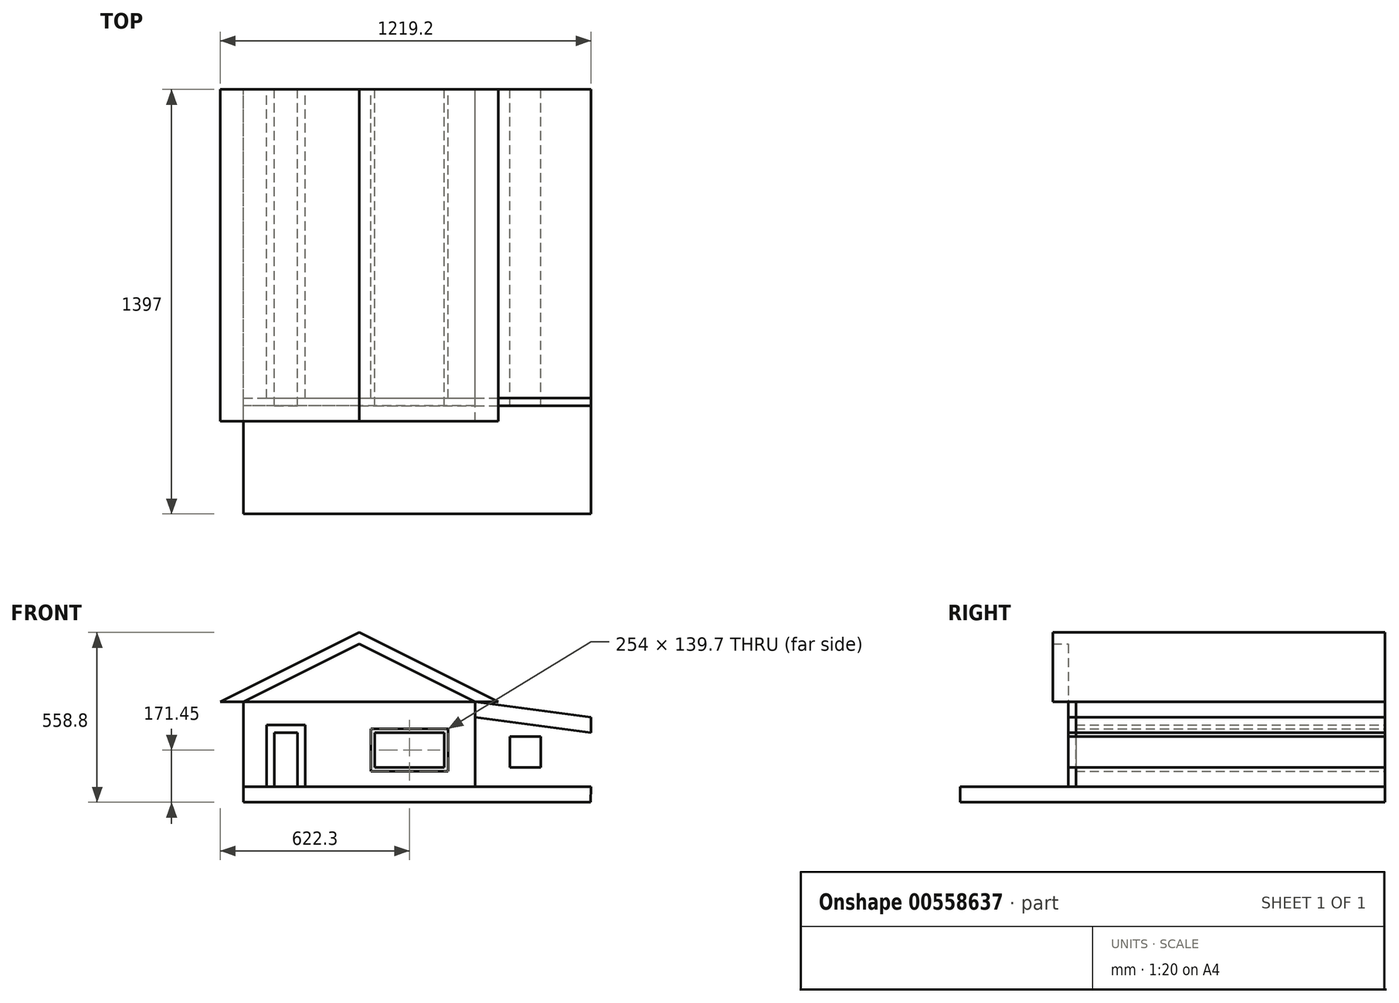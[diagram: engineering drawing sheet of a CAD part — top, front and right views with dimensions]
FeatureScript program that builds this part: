
annotation { "Feature Type Name" : "Feature", "Feature Type Description" : "" }
export const myFeature = defineFeature(function(context is Context, id is Id, definition is map)
    precondition{}
    {
        {
            var Q0;
            Q0=qCreatedBy(makeId("Front.planeOp"),FACE);
            var sketch = newSketch(context, id + "F0", { "sketchPlane" : qUnion([Q0])});
            skLineSegment(sketch, "E0", {"start": v(0, 0) * mm, "end": v(381, 0) * mm});
            skLineSegment(sketch, "E1", {"start": v(0, 0) * mm, "end": v(-381, 0) * mm});
            skLineSegment(sketch, "E2.bottom", {"start": v(-381, 0) * mm, "end": v(381, 0) * mm});
            skLineSegment(sketch, "E2.top", {"start": v(-381, -279.4) * mm, "end": v(381, -279.4) * mm});
            skLineSegment(sketch, "E2.left", {"start": v(-381, 0) * mm, "end": v(-381, -279.4) * mm});
            skLineSegment(sketch, "E2.right", {"start": v(381, 0) * mm, "end": v(381, -279.4) * mm});
            skLineSegment(sketch, "E3", {"start": v(0, 0) * mm, "end": v(0, 190.5) * mm});
            skLineSegment(sketch, "E4", {"start": v(0, 190.5) * mm, "end": v(-381, 0) * mm});
            skLineSegment(sketch, "E5", {"start": v(0, 190.5) * mm, "end": v(381, 0) * mm});
            skLineSegment(sketch, "E6", {"start": v(0, 190.5) * mm, "end": v(0, 228.6) * mm});
            skLineSegment(sketch, "E7", {"start": v(-381, 0) * mm, "end": v(-457.2, 0) * mm});
            skLineSegment(sketch, "E8", {"start": v(381, 0) * mm, "end": v(457.2, 0) * mm});
            skLineSegment(sketch, "E9", {"start": v(457.2, 0) * mm, "end": v(0, 228.6) * mm});
            skLineSegment(sketch, "E10", {"start": v(0, 228.6) * mm, "end": v(-457.2, 0) * mm});
            skLineSegment(sketch, "E11", {"start": v(-279.4, -279.4) * mm, "end": v(-279.4, -101.6) * mm});
            skLineSegment(sketch, "E12", {"start": v(-203.2, -279.4) * mm, "end": v(-203.2, -101.6) * mm});
            skLineSegment(sketch, "E13", {"start": v(-279.4, -101.6) * mm, "end": v(-203.2, -101.6) * mm});
            skLineSegment(sketch, "E14.0", {"start": v(-177.8, -279.4) * mm, "end": v(-177.8, -76.2) * mm});
            skLineSegment(sketch, "E14.1", {"start": v(-304.8, -76.2) * mm, "end": v(-177.8, -76.2) * mm});
            skLineSegment(sketch, "E14.2", {"start": v(-304.8, -279.4) * mm, "end": v(-304.8, -76.2) * mm});
            skLineSegment(sketch, "E15", {"start": v(381, 0) * mm, "end": v(381, -50.8) * mm});
            skLineSegment(sketch, "E16", {"start": v(381, -279.4) * mm, "end": v(762, -278.87) * mm});
            skLineSegment(sketch, "E17", {"start": v(762, -278.87) * mm, "end": v(762, -50.27) * mm});
            skLineSegment(sketch, "E18", {"start": v(381, 0) * mm, "end": v(762, -50.27) * mm});
            skLineSegment(sketch, "E19", {"start": v(381, -50.8) * mm, "end": v(762, -101.07) * mm});
            skLineSegment(sketch, "E20", {"start": v(381, -50.8) * mm, "end": v(381, 0) * mm});
            skLineSegment(sketch, "E21.0", {"start": v(-381, -330.2) * mm, "end": v(760.8, -330.2) * mm});
            skLineSegment(sketch, "E22", {"start": v(-381, -279.4) * mm, "end": v(-381, -330.2) * mm});
            skLineSegment(sketch, "E23", {"start": v(762, -278.87) * mm, "end": v(760.8, -330.2) * mm});
            skLineSegment(sketch, "E24.bottom", {"start": v(50.8, -101.6) * mm, "end": v(279.4, -101.6) * mm});
            skLineSegment(sketch, "E24.top", {"start": v(50.8, -215.9) * mm, "end": v(279.4, -215.9) * mm});
            skLineSegment(sketch, "E24.left", {"start": v(50.8, -101.6) * mm, "end": v(50.8, -215.9) * mm});
            skLineSegment(sketch, "E24.right", {"start": v(279.4, -101.6) * mm, "end": v(279.4, -215.9) * mm});
            skLineSegment(sketch, "E25.0", {"start": v(38.1, -88.9) * mm, "end": v(292.1, -88.9) * mm});
            skLineSegment(sketch, "E25.1", {"start": v(38.1, -88.9) * mm, "end": v(38.1, -228.6) * mm});
            skLineSegment(sketch, "E25.2", {"start": v(38.1, -228.6) * mm, "end": v(292.1, -228.6) * mm});
            skLineSegment(sketch, "E25.3", {"start": v(292.1, -88.9) * mm, "end": v(292.1, -228.6) * mm});
            skLineSegment(sketch, "E26.bottom", {"start": v(495.3, -114.14) * mm, "end": v(596.9, -114.14) * mm});
            skLineSegment(sketch, "E26.top", {"start": v(495.3, -215.74) * mm, "end": v(596.9, -215.74) * mm});
            skLineSegment(sketch, "E26.left", {"start": v(495.3, -114.14) * mm, "end": v(495.3, -215.74) * mm});
            skLineSegment(sketch, "E26.right", {"start": v(596.9, -114.14) * mm, "end": v(596.9, -215.74) * mm});
            skLineSegment(sketch, "E27.0", {"start": v(482.6, -101.44) * mm, "end": v(609.6, -101.44) * mm});
            skLineSegment(sketch, "E27.1", {"start": v(482.6, -101.44) * mm, "end": v(482.6, -228.44) * mm});
            skLineSegment(sketch, "E27.2", {"start": v(482.6, -228.44) * mm, "end": v(609.6, -228.44) * mm});
            skLineSegment(sketch, "E27.3", {"start": v(609.6, -101.44) * mm, "end": v(609.6, -228.44) * mm});
            skText(sketch, "E28", { "text": "Kyndal", "fontName": "OpenSans-Regular.ttf"});
            const initialGuessF0  = {"E28": [-0.49755, 0.25756, 1, 0, 0.1311]};
            skSetInitialGuess(sketch, initialGuessF0);
            skSolve(sketch);
        }
        {
            var Q0;
            Q0=makeQuery(id+"F0.imprint","IMPRINT",FACE,{"disambiguationData":[TD([[makeQuery(id+"F0.imprint","IMPRINT",EDGE,{"derivedFrom":sQuery(id+"F0.wireOp",EDGE,"E4")}),-1.0]])]});
            var Q1;
            Q1=makeQuery(id+"F0.imprint","IMPRINT",FACE,{"disambiguationData":[TD([[makeQuery(id+"F0.imprint","IMPRINT",EDGE,{"derivedFrom":sQuery(id+"F0.wireOp",EDGE,"E5")}),1.0]])]});
            extrude(context, id + "F1", {"entities" : qUnion([Q0, Q1]), "depth" : 1092.2 * mm, "offsetDistance" : 25.4 * mm});
        }
        {
            var Q0;
            {var subQ2=sQuery(id+"F0.wireOp",EDGE,"E3");Q0=makeQuery(id+"F0.imprint","IMPRINT",FACE,{"disambiguationData":[TD([[makeQuery(id+"F0.imprint","IMPRINT",EDGE,{"derivedFrom":subQ2}),1.0]])]});}
            var Q1;
            {var subQ2=sQuery(id+"F0.wireOp",EDGE,"E3");Q1=makeQuery(id+"F0.imprint","IMPRINT",FACE,{"disambiguationData":[TD([[makeQuery(id+"F0.imprint","IMPRINT",EDGE,{"derivedFrom":subQ2}),-1.0]])]});}
            extrude(context, id + "F2", {"entities" : qUnion([Q0, Q1]), "operationType" : NewBodyOperationType.ADD, "depth" : 1041.4 * mm, "offsetDistance" : 25.4 * mm});
        }
        {
            var Q0;
            {var subQ0=sQuery(id+"F0.wireOp",EDGE,"E18");Q0=makeQuery(id+"F0.imprint","IMPRINT",FACE,{"disambiguationData":[TD([[makeQuery(id+"F0.imprint","IMPRINT",EDGE,{"derivedFrom":subQ0}),-1.0]])]});}
            extrude(context, id + "F3", {"entities" : qUnion([Q0]), "depth" : 1041.4 * mm, "offsetDistance" : 25.4 * mm});
        }
        {
            var Q0;
            {var subQ2=sQuery(id+"F0.wireOp",EDGE,"E2.left");Q0=makeQuery(id+"F0.imprint","IMPRINT",FACE,{"disambiguationData":[TD([[makeQuery(id+"F0.imprint","IMPRINT",EDGE,{"derivedFrom":subQ2}),1.0]])]});}
            var Q1;
            Q1=makeQuery(id+"F0.imprint","IMPRINT",FACE,{"disambiguationData":[TD([[makeQuery(id+"F0.imprint","IMPRINT",EDGE,{"derivedFrom":sQuery(id+"F0.wireOp",EDGE,"E2.right")}),1.0]])]});
            extrude(context, id + "F4", {"entities" : qUnion([Q0, Q1]), "depth" : 1016 * mm, "offsetDistance" : 25.4 * mm});
        }
        {
            var Q0;
            {var subQ6=sQuery(id+"F0.wireOp",EDGE,"E16");Q0=makeQuery(id+"F0.imprint","IMPRINT",FACE,{"disambiguationData":[TD([[makeQuery(id+"F0.imprint","IMPRINT",EDGE,{"derivedFrom":subQ6}),-1.0]])]});}
            extrude(context, id + "F5", {"entities" : qUnion([Q0]), "operationType" : NewBodyOperationType.ADD, "depth" : 1397 * mm, "offsetDistance" : 25.4 * mm});
        }
        {
            var Q0;
            Q0=makeQuery(id+"F0.imprint","IMPRINT",FACE,{"disambiguationData":[TD([[makeQuery(id+"F0.imprint","IMPRINT",EDGE,{"derivedFrom":sQuery(id+"F0.wireOp",EDGE,"E26.bottom")}),-1.0]])]});
            var Q1;
            Q1=makeQuery(id+"F0.imprint","IMPRINT",FACE,{"disambiguationData":[TD([[makeQuery(id+"F0.imprint","IMPRINT",EDGE,{"derivedFrom":sQuery(id+"F0.wireOp",EDGE,"E24.bottom")}),-1.0]])]});
            var Q2;
            {var subQ0=sQuery(id+"F0.wireOp",EDGE,"E11");Q2=makeQuery(id+"F0.imprint","IMPRINT",FACE,{"disambiguationData":[TD([[makeQuery(id+"F0.imprint","IMPRINT",EDGE,{"derivedFrom":subQ0}),-1.0]])]});}
            extrude(context, id + "F6", {"entities" : qUnion([Q0, Q1, Q2]), "operationType" : NewBodyOperationType.ADD, "depth" : 1041.4 * mm, "offsetDistance" : 25.4 * mm});
        }
    });
